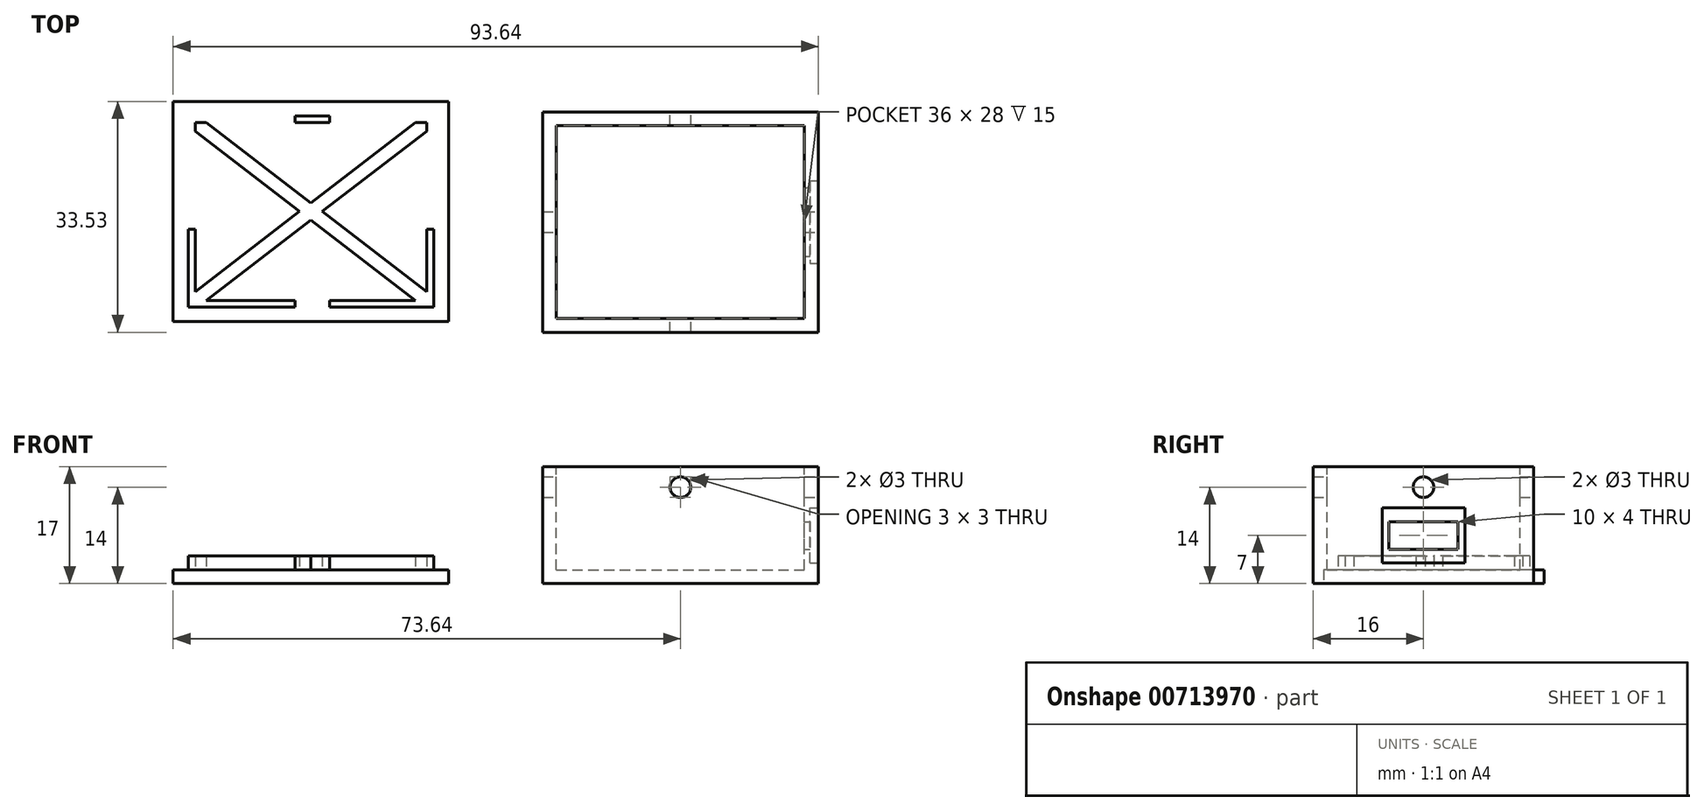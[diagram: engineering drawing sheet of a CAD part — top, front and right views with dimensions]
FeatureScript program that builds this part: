
annotation { "Feature Type Name" : "Feature", "Feature Type Description" : "" }
export const myFeature = defineFeature(function(context is Context, id is Id, definition is map)
    precondition{}
    {
        {
            var Q0;
            Q0=qCreatedBy(makeId("Top.planeOp"),FACE);
            var sketch = newSketch(context, id + "F0", { "sketchPlane" : qUnion([Q0])});
            skLineSegment(sketch, "E0.bottom", {"start": v(0, 0) * mm, "end": v(40, 0) * mm});
            skLineSegment(sketch, "E0.top", {"start": v(0, 32) * mm, "end": v(40, 32) * mm});
            skLineSegment(sketch, "E0.left", {"start": v(0, 0) * mm, "end": v(0, 32) * mm});
            skLineSegment(sketch, "E0.right", {"start": v(40, 0) * mm, "end": v(40, 32) * mm});
            skSolve(sketch);
        }
        {
            var Q0;
            Q0 = qSketchRegion(id + "F0", true);
            var Q1;
            Q1=makeQuery(id+"F0.imprint","IMPRINT",FACE,{"disambiguationData":[TD([[makeQuery(id+"F0.imprint","IMPRINT",EDGE,{"derivedFrom":sQuery(id+"F0.wireOp",EDGE,"E0.bottom")}),1.0]])]});
            extrude(context, id + "F1", {"entities" : qUnion([Q0, Q1]), "depth" : 17 * mm, "offsetDistance" : 25 * mm});
        }
        {
            var Q0;
            Q0=makeQuery(id+"F1.opExtrude","CAP_FACE",FACE,{"disambiguationData":[OSD([sQuery(id+"F0.wireOp",EDGE,"E0.bottom"),sQuery(id+"F0.wireOp",EDGE,"E0.top"),sQuery(id+"F0.wireOp",EDGE,"E0.left"),sQuery(id+"F0.wireOp",EDGE,"E0.right")])],"isStart":false});
            var sketch = newSketch(context, id + "F2", { "sketchPlane" : qUnion([Q0])});
            skLineSegment(sketch, "E1.bottom", {"start": v(2, 2) * mm, "end": v(38, 2) * mm});
            skLineSegment(sketch, "E1.top", {"start": v(2, 30) * mm, "end": v(38, 30) * mm});
            skLineSegment(sketch, "E1.left", {"start": v(2, 2) * mm, "end": v(2, 30) * mm});
            skLineSegment(sketch, "E1.right", {"start": v(38, 2) * mm, "end": v(38, 30) * mm});
            skSolve(sketch);
        }
        {
            var Q0;
            Q0=makeQuery(id+"F2.imprint","IMPRINT",FACE,{"disambiguationData":[TD([[makeQuery(id+"F2.imprint","IMPRINT",EDGE,{"derivedFrom":sQuery(id+"F2.wireOp",EDGE,"E1.bottom")}),1.0]])]});
            extrude(context, id + "F3", {"entities" : qUnion([Q0]), "operationType" : NewBodyOperationType.REMOVE, "oppositeDirection" : true, "depth" : 15 * mm, "offsetDistance" : 25 * mm});
        }
        {
            var Q0;
            Q0=makeQuery(id+"F1.opExtrude","SWEPT_FACE",FACE,{"disambiguationData":[OSD([sQuery(id+"F0.wireOp",EDGE,"E0.right")])]});
            var sketch = newSketch(context, id + "F4", { "sketchPlane" : qUnion([Q0])});
            skCircle(sketch, "E2", {"center": v(16, 14) * mm, "radius": 1.5 * mm});
            skLineSegment(sketch, "E3.bottom", {"start": v(11, 9) * mm, "end": v(21, 9) * mm});
            skLineSegment(sketch, "E3.top", {"start": v(11, 5) * mm, "end": v(21, 5) * mm});
            skLineSegment(sketch, "E3.left", {"start": v(11, 9) * mm, "end": v(11, 5) * mm});
            skLineSegment(sketch, "E3.right", {"start": v(21, 9) * mm, "end": v(21, 5) * mm});
            skLineSegment(sketch, "E4.bottom", {"start": v(22, 3) * mm, "end": v(10, 3) * mm});
            skLineSegment(sketch, "E4.top", {"start": v(22, 11) * mm, "end": v(10, 11) * mm});
            skLineSegment(sketch, "E4.left", {"start": v(22, 3) * mm, "end": v(22, 11) * mm});
            skLineSegment(sketch, "E4.right", {"start": v(10, 3) * mm, "end": v(10, 11) * mm});
            skSolve(sketch);
        }
        {
            var Q0;
            Q0=makeQuery(id+"F4.imprint","IMPRINT",FACE,{"disambiguationData":[TD([[makeQuery(id+"F4.imprint","IMPRINT",EDGE,{"derivedFrom":sQuery(id+"F4.wireOp",EDGE,"E2")}),1.0]])]});
            var Q1;
            Q1=sQuery(id+"F4.wireOp",EDGE,"E2");
            extrude(context, id + "F5", {"entities" : qUnion([Q0]), "operationType" : NewBodyOperationType.REMOVE, "surfaceEntities" : qUnion([Q1]), "endBound" : BoundingType.THROUGH_ALL, "oppositeDirection" : true, "depth" : 25 * mm, "offsetDistance" : 25 * mm});
        }
        {
            var Q0;
            Q0=makeQuery(id+"F1.opExtrude","SWEPT_FACE",FACE,{"disambiguationData":[OSD([sQuery(id+"F0.wireOp",EDGE,"E0.top")])]});
            var sketch = newSketch(context, id + "F6", { "sketchPlane" : qUnion([Q0])});
            skCircle(sketch, "E5", {"center": v(-20, 14) * mm, "radius": 1.5 * mm});
            skSolve(sketch);
        }
        {
            var Q0;
            Q0=makeQuery(id+"F6.imprint","IMPRINT",FACE,{"disambiguationData":[TD([[makeQuery(id+"F6.imprint","IMPRINT",EDGE,{"derivedFrom":sQuery(id+"F6.wireOp",EDGE,"E5")}),1.0]])]});
            var Q1;
            Q1=sQuery(id+"F6.wireOp",EDGE,"E5");
            extrude(context, id + "F7", {"entities" : qUnion([Q0]), "operationType" : NewBodyOperationType.REMOVE, "surfaceEntities" : qUnion([Q1]), "endBound" : BoundingType.THROUGH_ALL, "oppositeDirection" : true, "depth" : 25 * mm, "offsetDistance" : 25 * mm});
        }
        {
            var Q0;
            Q0=makeQuery(id+"F4.imprint","IMPRINT",FACE,{"disambiguationData":[TD([[makeQuery(id+"F4.imprint","IMPRINT",EDGE,{"derivedFrom":sQuery(id+"F4.wireOp",EDGE,"E3.bottom")}),-1.0]])]});
            extrude(context, id + "F8", {"entities" : qUnion([Q0]), "operationType" : NewBodyOperationType.REMOVE, "endBound" : BoundingType.UP_TO_NEXT, "oppositeDirection" : true, "depth" : 25 * mm, "offsetDistance" : 25 * mm});
        }
        {
            var Q0;
            Q0=qCreatedBy(makeId("Top.planeOp"),FACE);
            var sketch = newSketch(context, id + "F9", { "sketchPlane" : qUnion([Q0])});
            skLineSegment(sketch, "E6.bottom", {"start": v(-13.64, 33.53) * mm, "end": v(-53.64, 33.53) * mm});
            skLineSegment(sketch, "E6.top", {"start": v(-13.64, 1.53) * mm, "end": v(-53.64, 1.53) * mm});
            skLineSegment(sketch, "E6.left", {"start": v(-13.64, 33.53) * mm, "end": v(-13.64, 1.53) * mm});
            skLineSegment(sketch, "E6.right", {"start": v(-53.64, 33.53) * mm, "end": v(-53.64, 1.53) * mm});
            skSolve(sketch);
        }
        {
            var Q0;
            Q0=makeQuery(id+"F9.imprint","IMPRINT",FACE,{"disambiguationData":[TD([[makeQuery(id+"F9.imprint","IMPRINT",EDGE,{"derivedFrom":sQuery(id+"F9.wireOp",EDGE,"E6.bottom")}),1.0]])]});
            extrude(context, id + "F10", {"entities" : qUnion([Q0]), "depth" : 2 * mm, "offsetDistance" : 25 * mm});
        }
        {
            var Q0;
            Q0=makeQuery(id+"F10.opExtrude","CAP_FACE",FACE,{"disambiguationData":[OSD([sQuery(id+"F9.wireOp",EDGE,"E6.bottom"),sQuery(id+"F9.wireOp",EDGE,"E6.top"),sQuery(id+"F9.wireOp",EDGE,"E6.left"),sQuery(id+"F9.wireOp",EDGE,"E6.right")])],"isStart":false});
            var sketch = newSketch(context, id + "F11", { "sketchPlane" : qUnion([Q0])});
            skLineSegment(sketch, "E7.bottom", {"start": v(-51.44, 31.43) * mm, "end": v(-15.84, 31.43) * mm});
            skLineSegment(sketch, "E7.top", {"start": v(-51.44, 3.63) * mm, "end": v(-15.84, 3.63) * mm});
            skLineSegment(sketch, "E7.left", {"start": v(-51.44, 31.43) * mm, "end": v(-51.44, 3.63) * mm});
            skLineSegment(sketch, "E7.right", {"start": v(-15.84, 31.43) * mm, "end": v(-15.84, 3.63) * mm});
            skLineSegment(sketch, "E8.bottom", {"start": v(-50.44, 30.43) * mm, "end": v(-16.84, 30.43) * mm});
            skLineSegment(sketch, "E8.top", {"start": v(-50.44, 4.63) * mm, "end": v(-16.84, 4.63) * mm});
            skLineSegment(sketch, "E8.left", {"start": v(-50.44, 30.43) * mm, "end": v(-50.44, 4.63) * mm});
            skLineSegment(sketch, "E8.right", {"start": v(-16.84, 30.43) * mm, "end": v(-16.84, 4.63) * mm});
            skLineSegment(sketch, "E9", {"start": v(-50.44, 30.43) * mm, "end": v(-16.84, 4.63) * mm});
            skLineSegment(sketch, "E10", {"start": v(-16.84, 30.43) * mm, "end": v(-50.44, 4.63) * mm});
            skLineSegment(sketch, "E11", {"start": v(-50.44, 29.17) * mm, "end": v(-18.48, 4.63) * mm});
            skLineSegment(sketch, "E12", {"start": v(-48.8, 30.43) * mm, "end": v(-16.84, 5.89) * mm});
            skLineSegment(sketch, "E13", {"start": v(-50.44, 5.89) * mm, "end": v(-18.48, 30.43) * mm});
            skLineSegment(sketch, "E14", {"start": v(-16.84, 29.17) * mm, "end": v(-48.8, 4.63) * mm});
            skLineSegment(sketch, "E15.bottom", {"start": v(-35.94, 31.43) * mm, "end": v(-30.94, 31.43) * mm});
            skLineSegment(sketch, "E15.top", {"start": v(-35.94, 3.63) * mm, "end": v(-30.94, 3.63) * mm});
            skLineSegment(sketch, "E15.left", {"start": v(-35.94, 31.43) * mm, "end": v(-35.94, 3.63) * mm});
            skLineSegment(sketch, "E15.right", {"start": v(-30.94, 31.43) * mm, "end": v(-30.94, 3.63) * mm});
            skLineSegment(sketch, "E16.bottom", {"start": v(-51.44, 19.93) * mm, "end": v(-15.84, 19.93) * mm});
            skLineSegment(sketch, "E16.top", {"start": v(-51.44, 14.93) * mm, "end": v(-15.84, 14.93) * mm});
            skLineSegment(sketch, "E16.left", {"start": v(-51.44, 19.93) * mm, "end": v(-51.44, 14.93) * mm});
            skLineSegment(sketch, "E16.right", {"start": v(-15.84, 19.93) * mm, "end": v(-15.84, 14.93) * mm});
            skSolve(sketch);
        }
        {
            var Q0;
            Q0=makeQuery(id+"F11.imprint","IMPRINT",FACE,{"disambiguationData":[TD([[makeQuery(id+"F11.imprint","IMPRINT",EDGE,{"derivedFrom":sQuery(id+"F11.wireOp",EDGE,"E7.bottom")}),-1.0]])]});
            var Q1;
            {var subQ1=sQuery(id+"F11.wireOp",EDGE,"E8.left");var subQ3=sQuery(id+"F11.wireOp",EDGE,"E11");var subQ4=makeQuery(id+"F11.imprint","INTERSECT",VERTEX,{"derivedFrom":[subQ1,subQ3]});Q1=makeQuery(id+"F11.imprint","IMPRINT",FACE,{"disambiguationData":[TD([[makeQuery(id+"F11.imprint","IMPRINT",EDGE,{"disambiguationData":[TD([[subQ4,-1.0]])],"derivedFrom":subQ3}),1.0]])]});}
            var Q2;
            {var subQ1=sQuery(id+"F11.wireOp",EDGE,"E8.bottom");var subQ3=sQuery(id+"F11.wireOp",EDGE,"E12");var subQ4=makeQuery(id+"F11.imprint","INTERSECT",VERTEX,{"derivedFrom":[subQ1,subQ3]});Q2=makeQuery(id+"F11.imprint","IMPRINT",FACE,{"disambiguationData":[TD([[makeQuery(id+"F11.imprint","IMPRINT",EDGE,{"disambiguationData":[TD([[subQ4,-1.0]])],"derivedFrom":subQ3}),-1.0]])]});}
            var Q3;
            {var subQ0=sQuery(id+"F11.wireOp",EDGE,"E13");var subQ1=sQuery(id+"F11.wireOp",EDGE,"E9");var subQ2=makeQuery(id+"F11.imprint","INTERSECT",VERTEX,{"derivedFrom":[subQ1,subQ0]});Q3=makeQuery(id+"F11.imprint","IMPRINT",FACE,{"disambiguationData":[TD([[makeQuery(id+"F11.imprint","IMPRINT",EDGE,{"disambiguationData":[TD([[subQ2,-1.0]])],"derivedFrom":subQ1}),1.0]])]});}
            var Q4;
            {var subQ0=sQuery(id+"F11.wireOp",EDGE,"E10");var subQ1=sQuery(id+"F11.wireOp",EDGE,"E9");var subQ2=makeQuery(id+"F11.imprint","INTERSECT",VERTEX,{"derivedFrom":[subQ1,subQ0]});Q4=makeQuery(id+"F11.imprint","IMPRINT",FACE,{"disambiguationData":[TD([[makeQuery(id+"F11.imprint","IMPRINT",EDGE,{"disambiguationData":[TD([[subQ2,-1.0]])],"derivedFrom":subQ1}),1.0]])]});}
            var Q5;
            {var subQ0=sQuery(id+"F11.wireOp",EDGE,"E13");var subQ1=sQuery(id+"F11.wireOp",EDGE,"E9");var subQ2=makeQuery(id+"F11.imprint","INTERSECT",VERTEX,{"derivedFrom":[subQ1,subQ0]});Q5=makeQuery(id+"F11.imprint","IMPRINT",FACE,{"disambiguationData":[TD([[makeQuery(id+"F11.imprint","IMPRINT",EDGE,{"disambiguationData":[TD([[subQ2,-1.0]])],"derivedFrom":subQ1}),-1.0]])]});}
            var Q6;
            {var subQ0=sQuery(id+"F11.wireOp",EDGE,"E10");var subQ1=sQuery(id+"F11.wireOp",EDGE,"E9");var subQ2=makeQuery(id+"F11.imprint","INTERSECT",VERTEX,{"derivedFrom":[subQ1,subQ0]});Q6=makeQuery(id+"F11.imprint","IMPRINT",FACE,{"disambiguationData":[TD([[makeQuery(id+"F11.imprint","IMPRINT",EDGE,{"disambiguationData":[TD([[subQ2,-1.0]])],"derivedFrom":subQ1}),-1.0]])]});}
            var Q7;
            {var subQ0=sQuery(id+"F11.wireOp",EDGE,"E10");var subQ5=sQuery(id+"F11.wireOp",EDGE,"E12");var subQ6=makeQuery(id+"F11.imprint","INTERSECT",VERTEX,{"derivedFrom":[subQ0,subQ5]});Q7=makeQuery(id+"F11.imprint","IMPRINT",FACE,{"disambiguationData":[TD([[makeQuery(id+"F11.imprint","IMPRINT",EDGE,{"disambiguationData":[TD([[subQ6,-1.0]])],"derivedFrom":subQ5}),1.0]])]});}
            var Q8;
            {var subQ0=sQuery(id+"F11.wireOp",EDGE,"E10");var subQ5=sQuery(id+"F11.wireOp",EDGE,"E12");var subQ6=makeQuery(id+"F11.imprint","INTERSECT",VERTEX,{"derivedFrom":[subQ0,subQ5]});Q8=makeQuery(id+"F11.imprint","IMPRINT",FACE,{"disambiguationData":[TD([[makeQuery(id+"F11.imprint","IMPRINT",EDGE,{"disambiguationData":[TD([[subQ6,1.0]])],"derivedFrom":subQ5}),1.0]])]});}
            var Q9;
            {var subQ0=sQuery(id+"F11.wireOp",EDGE,"E10");var subQ5=sQuery(id+"F11.wireOp",EDGE,"E11");var subQ7=makeQuery(id+"F11.imprint","INTERSECT",VERTEX,{"derivedFrom":[subQ0,subQ5]});Q9=makeQuery(id+"F11.imprint","IMPRINT",FACE,{"disambiguationData":[TD([[makeQuery(id+"F11.imprint","IMPRINT",EDGE,{"disambiguationData":[TD([[subQ7,1.0]])],"derivedFrom":subQ5}),-1.0]])]});}
            var Q10;
            {var subQ0=sQuery(id+"F11.wireOp",EDGE,"E10");var subQ5=sQuery(id+"F11.wireOp",EDGE,"E11");var subQ6=makeQuery(id+"F11.imprint","INTERSECT",VERTEX,{"derivedFrom":[subQ0,subQ5]});Q10=makeQuery(id+"F11.imprint","IMPRINT",FACE,{"disambiguationData":[TD([[makeQuery(id+"F11.imprint","IMPRINT",EDGE,{"disambiguationData":[TD([[subQ6,-1.0]])],"derivedFrom":subQ5}),-1.0]])]});}
            var Q11;
            {var subQ1=sQuery(id+"F11.wireOp",EDGE,"E8.top");var subQ3=sQuery(id+"F11.wireOp",EDGE,"E11");var subQ4=makeQuery(id+"F11.imprint","INTERSECT",VERTEX,{"derivedFrom":[subQ1,subQ3]});Q11=makeQuery(id+"F11.imprint","IMPRINT",FACE,{"disambiguationData":[TD([[makeQuery(id+"F11.imprint","IMPRINT",EDGE,{"disambiguationData":[TD([[subQ4,1.0]])],"derivedFrom":subQ3}),1.0]])]});}
            var Q12;
            {var subQ1=sQuery(id+"F11.wireOp",EDGE,"E8.right");var subQ3=sQuery(id+"F11.wireOp",EDGE,"E12");var subQ4=makeQuery(id+"F11.imprint","INTERSECT",VERTEX,{"derivedFrom":[subQ1,subQ3]});Q12=makeQuery(id+"F11.imprint","IMPRINT",FACE,{"disambiguationData":[TD([[makeQuery(id+"F11.imprint","IMPRINT",EDGE,{"disambiguationData":[TD([[subQ4,1.0]])],"derivedFrom":subQ3}),-1.0]])]});}
            var Q13;
            {var subQ0=sQuery(id+"F11.wireOp",EDGE,"E15.left");var subQ1=sQuery(id+"F11.wireOp",EDGE,"E10");var subQ2=makeQuery(id+"F11.imprint","INTERSECT",VERTEX,{"derivedFrom":[subQ1,subQ0]});Q13=makeQuery(id+"F11.imprint","IMPRINT",FACE,{"disambiguationData":[TD([[makeQuery(id+"F11.imprint","IMPRINT",EDGE,{"disambiguationData":[TD([[subQ2,-1.0]])],"derivedFrom":subQ1}),-1.0]])]});}
            var Q14;
            {var subQ0=sQuery(id+"F11.wireOp",EDGE,"E16.bottom");var subQ1=sQuery(id+"F11.wireOp",EDGE,"E9");var subQ2=makeQuery(id+"F11.imprint","INTERSECT",VERTEX,{"derivedFrom":[subQ1,subQ0]});Q14=makeQuery(id+"F11.imprint","IMPRINT",FACE,{"disambiguationData":[TD([[makeQuery(id+"F11.imprint","IMPRINT",EDGE,{"disambiguationData":[TD([[subQ2,-1.0]])],"derivedFrom":subQ1}),-1.0]])]});}
            var Q15;
            {var subQ0=sQuery(id+"F11.wireOp",EDGE,"E15.left");var subQ1=sQuery(id+"F11.wireOp",EDGE,"E9");var subQ2=makeQuery(id+"F11.imprint","INTERSECT",VERTEX,{"derivedFrom":[subQ1,subQ0]});Q15=makeQuery(id+"F11.imprint","IMPRINT",FACE,{"disambiguationData":[TD([[makeQuery(id+"F11.imprint","IMPRINT",EDGE,{"disambiguationData":[TD([[subQ2,-1.0]])],"derivedFrom":subQ1}),-1.0]])]});}
            var Q16;
            {var subQ0=sQuery(id+"F11.wireOp",EDGE,"E15.left");var subQ1=sQuery(id+"F11.wireOp",EDGE,"E9");var subQ2=makeQuery(id+"F11.imprint","INTERSECT",VERTEX,{"derivedFrom":[subQ1,subQ0]});Q16=makeQuery(id+"F11.imprint","IMPRINT",FACE,{"disambiguationData":[TD([[makeQuery(id+"F11.imprint","IMPRINT",EDGE,{"disambiguationData":[TD([[subQ2,-1.0]])],"derivedFrom":subQ1}),1.0]])]});}
            var Q17;
            {var subQ0=sQuery(id+"F11.wireOp",EDGE,"E15.left");var subQ1=sQuery(id+"F11.wireOp",EDGE,"E12");var subQ2=makeQuery(id+"F11.imprint","INTERSECT",VERTEX,{"derivedFrom":[subQ1,subQ0]});Q17=makeQuery(id+"F11.imprint","IMPRINT",FACE,{"disambiguationData":[TD([[makeQuery(id+"F11.imprint","IMPRINT",EDGE,{"disambiguationData":[TD([[subQ2,-1.0]])],"derivedFrom":subQ1}),-1.0]])]});}
            var Q18;
            {var subQ0=sQuery(id+"F11.wireOp",EDGE,"E15.left");var subQ1=sQuery(id+"F11.wireOp",EDGE,"E10");var subQ2=makeQuery(id+"F11.imprint","INTERSECT",VERTEX,{"derivedFrom":[subQ1,subQ0]});Q18=makeQuery(id+"F11.imprint","IMPRINT",FACE,{"disambiguationData":[TD([[makeQuery(id+"F11.imprint","IMPRINT",EDGE,{"disambiguationData":[TD([[subQ2,-1.0]])],"derivedFrom":subQ1}),1.0]])]});}
            var Q19;
            {var subQ1=sQuery(id+"F11.wireOp",EDGE,"E9");var subQ5=sQuery(id+"F11.wireOp",EDGE,"E14");var subQ6=makeQuery(id+"F11.imprint","INTERSECT",VERTEX,{"derivedFrom":[subQ1,subQ5]});Q19=makeQuery(id+"F11.imprint","IMPRINT",FACE,{"disambiguationData":[TD([[makeQuery(id+"F11.imprint","IMPRINT",EDGE,{"disambiguationData":[TD([[subQ6,-1.0]])],"derivedFrom":subQ1}),-1.0]])]});}
            var Q20;
            {var subQ0=sQuery(id+"F11.wireOp",EDGE,"E14");var subQ1=sQuery(id+"F11.wireOp",EDGE,"E9");var subQ2=makeQuery(id+"F11.imprint","INTERSECT",VERTEX,{"derivedFrom":[subQ1,subQ0]});Q20=makeQuery(id+"F11.imprint","IMPRINT",FACE,{"disambiguationData":[TD([[makeQuery(id+"F11.imprint","IMPRINT",EDGE,{"disambiguationData":[TD([[subQ2,-1.0]])],"derivedFrom":subQ1}),1.0]])]});}
            var Q21;
            {var subQ0=sQuery(id+"F11.wireOp",EDGE,"E15.right");var subQ1=sQuery(id+"F11.wireOp",EDGE,"E9");var subQ2=makeQuery(id+"F11.imprint","INTERSECT",VERTEX,{"derivedFrom":[subQ1,subQ0]});Q21=makeQuery(id+"F11.imprint","IMPRINT",FACE,{"disambiguationData":[TD([[makeQuery(id+"F11.imprint","IMPRINT",EDGE,{"disambiguationData":[TD([[subQ2,-1.0]])],"derivedFrom":subQ1}),1.0]])]});}
            var Q22;
            {var subQ0=sQuery(id+"F11.wireOp",EDGE,"E15.right");var subQ1=sQuery(id+"F11.wireOp",EDGE,"E9");var subQ2=makeQuery(id+"F11.imprint","INTERSECT",VERTEX,{"derivedFrom":[subQ1,subQ0]});Q22=makeQuery(id+"F11.imprint","IMPRINT",FACE,{"disambiguationData":[TD([[makeQuery(id+"F11.imprint","IMPRINT",EDGE,{"disambiguationData":[TD([[subQ2,-1.0]])],"derivedFrom":subQ1}),-1.0]])]});}
            var Q23;
            {var subQ0=sQuery(id+"F11.wireOp",EDGE,"E16.top");var subQ1=sQuery(id+"F11.wireOp",EDGE,"E11");var subQ2=makeQuery(id+"F11.imprint","INTERSECT",VERTEX,{"derivedFrom":[subQ1,subQ0]});Q23=makeQuery(id+"F11.imprint","IMPRINT",FACE,{"disambiguationData":[TD([[makeQuery(id+"F11.imprint","IMPRINT",EDGE,{"disambiguationData":[TD([[subQ2,-1.0]])],"derivedFrom":subQ1}),1.0]])]});}
            var Q24;
            {var subQ0=sQuery(id+"F11.wireOp",EDGE,"E16.bottom");var subQ1=sQuery(id+"F11.wireOp",EDGE,"E9");var subQ2=makeQuery(id+"F11.imprint","INTERSECT",VERTEX,{"derivedFrom":[subQ1,subQ0]});Q24=makeQuery(id+"F11.imprint","IMPRINT",FACE,{"disambiguationData":[TD([[makeQuery(id+"F11.imprint","IMPRINT",EDGE,{"disambiguationData":[TD([[subQ2,-1.0]])],"derivedFrom":subQ1}),1.0]])]});}
            var Q25;
            {var subQ0=sQuery(id+"F11.wireOp",EDGE,"E16.bottom");var subQ1=sQuery(id+"F11.wireOp",EDGE,"E10");var subQ2=makeQuery(id+"F11.imprint","INTERSECT",VERTEX,{"derivedFrom":[subQ1,subQ0]});Q25=makeQuery(id+"F11.imprint","IMPRINT",FACE,{"disambiguationData":[TD([[makeQuery(id+"F11.imprint","IMPRINT",EDGE,{"disambiguationData":[TD([[subQ2,-1.0]])],"derivedFrom":subQ1}),1.0]])]});}
            var Q26;
            {var subQ0=sQuery(id+"F11.wireOp",EDGE,"E16.bottom");var subQ1=sQuery(id+"F11.wireOp",EDGE,"E10");var subQ2=makeQuery(id+"F11.imprint","INTERSECT",VERTEX,{"derivedFrom":[subQ1,subQ0]});Q26=makeQuery(id+"F11.imprint","IMPRINT",FACE,{"disambiguationData":[TD([[makeQuery(id+"F11.imprint","IMPRINT",EDGE,{"disambiguationData":[TD([[subQ2,-1.0]])],"derivedFrom":subQ1}),-1.0]])]});}
            var Q27;
            {var subQ0=sQuery(id+"F11.wireOp",EDGE,"E16.bottom");var subQ1=sQuery(id+"F11.wireOp",EDGE,"E13");var subQ2=makeQuery(id+"F11.imprint","INTERSECT",VERTEX,{"derivedFrom":[subQ1,subQ0]});Q27=makeQuery(id+"F11.imprint","IMPRINT",FACE,{"disambiguationData":[TD([[makeQuery(id+"F11.imprint","IMPRINT",EDGE,{"disambiguationData":[TD([[subQ2,-1.0]])],"derivedFrom":subQ1}),-1.0]])]});}
            var Q28;
            {var subQ1=sQuery(id+"F11.wireOp",EDGE,"E13");var subQ6=sQuery(id+"F11.wireOp",EDGE,"E8.bottom");var subQ9=makeQuery(id+"F11.imprint","INTERSECT",VERTEX,{"derivedFrom":[subQ6,subQ1]});Q28=makeQuery(id+"F11.imprint","IMPRINT",FACE,{"disambiguationData":[TD([[makeQuery(id+"F11.imprint","IMPRINT",EDGE,{"disambiguationData":[TD([[subQ9,1.0]])],"derivedFrom":subQ1}),-1.0]])]});}
            var Q29;
            {var subQ1=sQuery(id+"F11.wireOp",EDGE,"E8.right");var subQ3=sQuery(id+"F11.wireOp",EDGE,"E14");var subQ4=makeQuery(id+"F11.imprint","INTERSECT",VERTEX,{"derivedFrom":[subQ1,subQ3]});Q29=makeQuery(id+"F11.imprint","IMPRINT",FACE,{"disambiguationData":[TD([[makeQuery(id+"F11.imprint","IMPRINT",EDGE,{"disambiguationData":[TD([[subQ4,-1.0]])],"derivedFrom":subQ3}),-1.0]])]});}
            var Q30;
            {var subQ1=sQuery(id+"F11.wireOp",EDGE,"E14");var subQ5=sQuery(id+"F11.wireOp",EDGE,"E8.top");var subQ6=makeQuery(id+"F11.imprint","INTERSECT",VERTEX,{"derivedFrom":[subQ5,subQ1]});Q30=makeQuery(id+"F11.imprint","IMPRINT",FACE,{"disambiguationData":[TD([[makeQuery(id+"F11.imprint","IMPRINT",EDGE,{"disambiguationData":[TD([[subQ6,1.0]])],"derivedFrom":subQ1}),-1.0]])]});}
            var Q31;
            {var subQ1=sQuery(id+"F11.wireOp",EDGE,"E8.left");var subQ3=sQuery(id+"F11.wireOp",EDGE,"E13");var subQ4=makeQuery(id+"F11.imprint","INTERSECT",VERTEX,{"derivedFrom":[subQ1,subQ3]});Q31=makeQuery(id+"F11.imprint","IMPRINT",FACE,{"disambiguationData":[TD([[makeQuery(id+"F11.imprint","IMPRINT",EDGE,{"disambiguationData":[TD([[subQ4,-1.0]])],"derivedFrom":subQ3}),-1.0]])]});}
            var Q32;
            {var subQ0=sQuery(id+"F11.wireOp",EDGE,"E8.top");var subQ1=makeQuery(id+"F11.imprint","INTERSECT",VERTEX,{"derivedFrom":[subQ0,sQuery(id+"F11.wireOp",EDGE,"E14")]});Q32=makeQuery(id+"F11.imprint","IMPRINT",FACE,{"disambiguationData":[TD([[makeQuery(id+"F11.imprint","IMPRINT",EDGE,{"disambiguationData":[TD([[subQ1,-1.0]])],"derivedFrom":subQ0}),-1.0]])]});}
            var Q33;
            {var subQ0=sQuery(id+"F11.wireOp",EDGE,"E8.top");var subQ1=makeQuery(id+"F11.imprint","INTERSECT",VERTEX,{"derivedFrom":[subQ0,sQuery(id+"F11.wireOp",EDGE,"E11")]});Q33=makeQuery(id+"F11.imprint","IMPRINT",FACE,{"disambiguationData":[TD([[makeQuery(id+"F11.imprint","IMPRINT",EDGE,{"disambiguationData":[TD([[subQ1,1.0]])],"derivedFrom":subQ0}),-1.0]])]});}
            var Q34;
            {var subQ0=sQuery(id+"F11.wireOp",EDGE,"E16.top");var subQ1=sQuery(id+"F11.wireOp",EDGE,"E14");var subQ2=makeQuery(id+"F11.imprint","INTERSECT",VERTEX,{"derivedFrom":[subQ1,subQ0]});Q34=makeQuery(id+"F11.imprint","IMPRINT",FACE,{"disambiguationData":[TD([[makeQuery(id+"F11.imprint","IMPRINT",EDGE,{"disambiguationData":[TD([[subQ2,-1.0]])],"derivedFrom":subQ1}),-1.0]])]});}
            extrude(context, id + "F12", {"entities" : qUnion([Q0, Q1, Q2, Q3, Q4, Q5, Q6, Q7, Q8, Q9, Q10, Q11, Q12, Q13, Q14, Q15, Q16, Q17, Q18, Q19, Q20, Q21, Q22, Q23, Q24, Q25, Q26, Q27, Q28, Q29, Q30, Q31, Q32, Q33, Q34]), "operationType" : NewBodyOperationType.ADD, "depth" : 2 * mm, "offsetDistance" : 25 * mm});
        }
        {
            var Q0;
            Q0=makeQuery(id+"F4.imprint","IMPRINT",FACE,{"disambiguationData":[TD([[makeQuery(id+"F4.imprint","IMPRINT",EDGE,{"derivedFrom":sQuery(id+"F4.wireOp",EDGE,"E3.bottom")}),1.0]])]});
            extrude(context, id + "F13", {"entities" : qUnion([Q0]), "operationType" : NewBodyOperationType.REMOVE, "oppositeDirection" : true, "depth" : 1.2 * mm, "offsetDistance" : 25 * mm});
        }
    });
